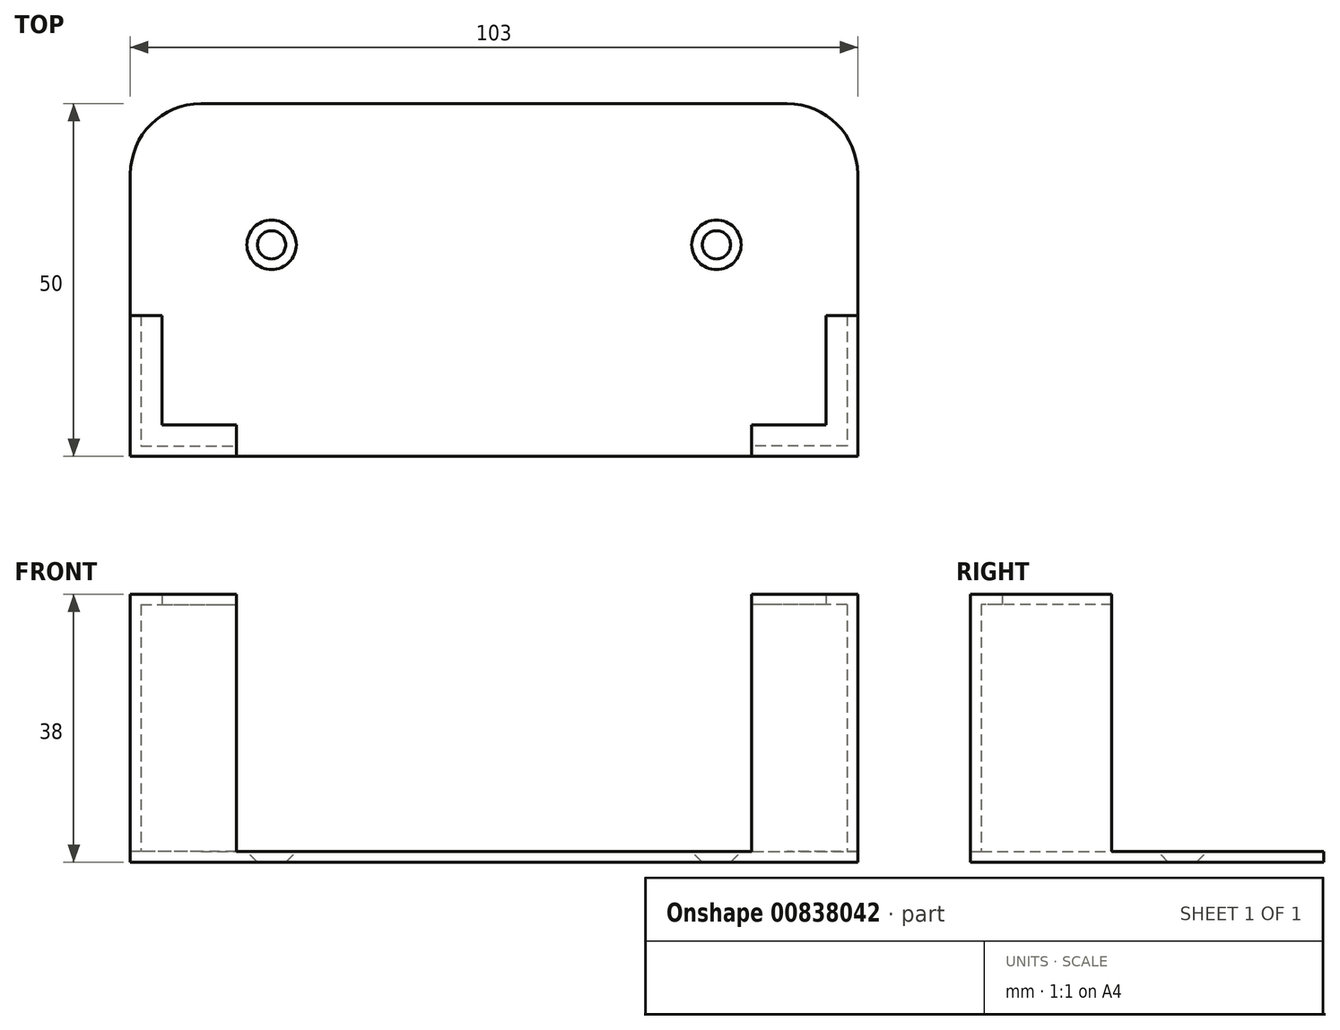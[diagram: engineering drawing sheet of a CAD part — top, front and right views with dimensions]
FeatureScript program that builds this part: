
annotation { "Feature Type Name" : "Feature", "Feature Type Description" : "" }
export const myFeature = defineFeature(function(context is Context, id is Id, definition is map)
    precondition{}
    {
        {
            assignVariable(context, id + "F0", {"name" : "thickness", "anyValue" : 1.5});
        }
        {
            assignVariable(context, id + "F1", {"name" : "deviceDepth", "anyValue" : 35});
        }
        {
            var Q0;
            Q0=qCreatedBy(makeId("Top.planeOp"),FACE);
            var sketch = newSketch(context, id + "F2", { "sketchPlane" : qUnion([Q0])});
            skLineSegment(sketch, "E0.bottom", {"start": v(0, 0) * mm, "end": v(103, 0) * mm});
            skLineSegment(sketch, "E0.top", {"start": v(10, 50) * mm, "end": v(93, 50) * mm});
            skLineSegment(sketch, "E0.left", {"start": v(0, 0) * mm, "end": v(0, 40) * mm});
            skLineSegment(sketch, "E0.right", {"start": v(103, 0) * mm, "end": v(103, 40) * mm});
            skPoint(sketch, "E1.visualSharp", {"position": v(0, 50) * mm});
            skArc(sketch, "E1.filletArc", {"start": v(10, 50) * mm, "mid": v(2.93, 47.07) * mm, "end": v(0, 40) * mm});
            skPoint(sketch, "E2.visualSharp", {"position": v(103, 50) * mm});
            skArc(sketch, "E2.filletArc", {"start": v(103, 40) * mm, "mid": v(100.07, 47.07) * mm, "end": v(93, 50) * mm});
            skPoint(sketch, "E3", {"position": v(20, 30) * mm});
            skLineSegment(sketch, "E4", {"start": v(51.5, 50) * mm, "end": v(51.5, 0) * mm, "construction": true});
            skPoint(sketch, "E5.MirrorP", {"position": v(83, 30) * mm});
            skLineSegment(sketch, "E6", {"start": v(0, 20) * mm, "end": v(4.5, 20) * mm});
            skLineSegment(sketch, "E7", {"start": v(4.5, 20) * mm, "end": v(4.5, 4.5) * mm});
            skLineSegment(sketch, "E8", {"start": v(4.5, 4.5) * mm, "end": v(15, 4.5) * mm});
            skLineSegment(sketch, "E9", {"start": v(15, 4.5) * mm, "end": v(15, 0) * mm});
            skLineSegment(sketch, "E10", {"start": v(1.5, 20) * mm, "end": v(1.5, 1.5) * mm});
            skLineSegment(sketch, "E11", {"start": v(1.5, 1.5) * mm, "end": v(15, 1.5) * mm});
            skLineSegment(sketch, "E12.MirrorCS", {"start": v(103, 20) * mm, "end": v(98.5, 20) * mm});
            skLineSegment(sketch, "E13.MirrorCS", {"start": v(103, 0) * mm, "end": v(0, 0) * mm});
            skLineSegment(sketch, "E14.MirrorCS", {"start": v(88, 4.5) * mm, "end": v(88, 0) * mm});
            skLineSegment(sketch, "E15.MirrorCS", {"start": v(98.5, 20) * mm, "end": v(98.5, 4.5) * mm});
            skLineSegment(sketch, "E16.MirrorCS", {"start": v(101.5, 20) * mm, "end": v(101.5, 1.5) * mm});
            skLineSegment(sketch, "E17.MirrorCS", {"start": v(101.5, 1.5) * mm, "end": v(88, 1.5) * mm});
            skLineSegment(sketch, "E18.MirrorCS", {"start": v(98.5, 4.5) * mm, "end": v(88, 4.5) * mm});
            skSolve(sketch);
        }
        {
            var Q0;
            Q0=makeQuery(id+"F2.imprint","IMPRINT",FACE,{"disambiguationData":[TD([[makeQuery(id+"F2.imprint","IMPRINT",EDGE,{"derivedFrom":sQuery(id+"F2.wireOp",EDGE,"E0.top")}),-1.0]])]});
            var Q1;
            {var subQ3=sQuery(id+"F2.wireOp",EDGE,"E7");Q1=makeQuery(id+"F2.imprint","IMPRINT",FACE,{"disambiguationData":[TD([[makeQuery(id+"F2.imprint","IMPRINT",EDGE,{"derivedFrom":subQ3}),-1.0]])]});}
            var Q2;
            {var subQ0=sQuery(id+"F2.wireOp",EDGE,"E15.MirrorCS");Q2=makeQuery(id+"F2.imprint","IMPRINT",FACE,{"disambiguationData":[TD([[makeQuery(id+"F2.imprint","IMPRINT",EDGE,{"derivedFrom":subQ0}),1.0]])]});}
            var Q3;
            {var subQ8=sQuery(id+"F2.wireOp",EDGE,"E16.MirrorCS");Q3=makeQuery(id+"F2.imprint","IMPRINT",FACE,{"disambiguationData":[TD([[makeQuery(id+"F2.imprint","IMPRINT",EDGE,{"derivedFrom":subQ8}),1.0]])]});}
            var Q4;
            {var subQ7=sQuery(id+"F2.wireOp",EDGE,"E10");Q4=makeQuery(id+"F2.imprint","IMPRINT",FACE,{"disambiguationData":[TD([[makeQuery(id+"F2.imprint","IMPRINT",EDGE,{"derivedFrom":subQ7}),-1.0]])]});}
            extrude(context, id + "F3", {"entities" : qUnion([Q0, Q1, Q2, Q3, Q4]), "depth" : (getVariable(context, 'thickness')) * mm, "offsetDistance" : 25 * mm});
        }
        {
            var Q0;
            {var subQ7=sQuery(id+"F2.wireOp",EDGE,"E10");Q0=makeQuery(id+"F2.imprint","IMPRINT",FACE,{"disambiguationData":[TD([[makeQuery(id+"F2.imprint","IMPRINT",EDGE,{"derivedFrom":subQ7}),-1.0]])]});}
            var Q1;
            {var subQ8=sQuery(id+"F2.wireOp",EDGE,"E16.MirrorCS");Q1=makeQuery(id+"F2.imprint","IMPRINT",FACE,{"disambiguationData":[TD([[makeQuery(id+"F2.imprint","IMPRINT",EDGE,{"derivedFrom":subQ8}),1.0]])]});}
            extrude(context, id + "F4", {"entities" : qUnion([Q0, Q1]), "operationType" : NewBodyOperationType.ADD, "depth" : (getVariable(context, 'thickness') * 2 + getVariable(context, 'deviceDepth')) * mm, "offsetDistance" : 25 * mm});
        }
        {
            var Q0;
            {var subQ0=sQuery(id+"F2.wireOp",EDGE,"E15.MirrorCS");Q0=makeQuery(id+"F2.imprint","IMPRINT",FACE,{"disambiguationData":[TD([[makeQuery(id+"F2.imprint","IMPRINT",EDGE,{"derivedFrom":subQ0}),1.0]])]});}
            var Q1;
            {var subQ3=sQuery(id+"F2.wireOp",EDGE,"E7");Q1=makeQuery(id+"F2.imprint","IMPRINT",FACE,{"disambiguationData":[TD([[makeQuery(id+"F2.imprint","IMPRINT",EDGE,{"derivedFrom":subQ3}),-1.0]])]});}
            extrude(context, id + "F5", {"entities" : qUnion([Q0, Q1]), "operationType" : NewBodyOperationType.ADD, "depth" : (getVariable(context, 'thickness') * 2 + getVariable(context, 'deviceDepth')) * mm, "offsetDistance" : 25 * mm, "hasSecondDirection" : true, "secondDirectionOppositeDirection" : false, "secondDirectionDepth" : (getVariable(context, 'thickness') + getVariable(context, 'deviceDepth')) * mm});
        }
        {
            var Q0;
            Q0=makeQuery(id+"F3.opExtrude","CAP_FACE",FACE,{"disambiguationData":[OSD([sQuery(id+"F2.wireOp",EDGE,"E0.top"),sQuery(id+"F2.wireOp",EDGE,"E0.left"),sQuery(id+"F2.wireOp",EDGE,"E1.filletArc"),sQuery(id+"F2.wireOp",EDGE,"E2.filletArc"),sQuery(id+"F2.wireOp",EDGE,"E13.MirrorCS"),sQuery(id+"F2.wireOp",EDGE,"E0.right")])],"isStart":false});
            var sketch = newSketch(context, id + "F6", { "sketchPlane" : qUnion([Q0])});
            skPoint(sketch, "E19", {"position": v(20, 30) * mm});
            skPoint(sketch, "E20", {"position": v(83, 30) * mm});
            skSolve(sketch);
        }
        {
            var Q0;
            Q0=sQuery(id+"F6.wireOp",VERTEX,"E19");
            var Q1;
            Q1=sQuery(id+"F6.wireOp",VERTEX,"E20");
            var Q2;
            Q2=makeQuery(id+"F3.opExtrude","SWEPT_BODY",BODY,{"disambiguationData":[OSD([sQuery(id+"F2.wireOp",EDGE,"E0.top"),sQuery(id+"F2.wireOp",EDGE,"E0.left"),sQuery(id+"F2.wireOp",EDGE,"E1.filletArc"),sQuery(id+"F2.wireOp",EDGE,"E2.filletArc"),sQuery(id+"F2.wireOp",EDGE,"E13.MirrorCS"),sQuery(id+"F2.wireOp",EDGE,"E0.right")])]});
            hole(context, id + "F7", {"style" : HoleStyle.C_SINK, "endStyle" : HoleEndStyle.THROUGH, "holeDiameter" : 4 * mm, "cSinkDiameter" : 7 * mm, "cSinkAngle" : 90 * degree, "majorDiameter" : 5 * mm, "isTappedThrough" : true, "tappedDepth" : 12 * mm, "tapClearance" : 3, "locations" : qUnion([Q0, Q1]), "scope" : qUnion([Q2])});
        }
    });
